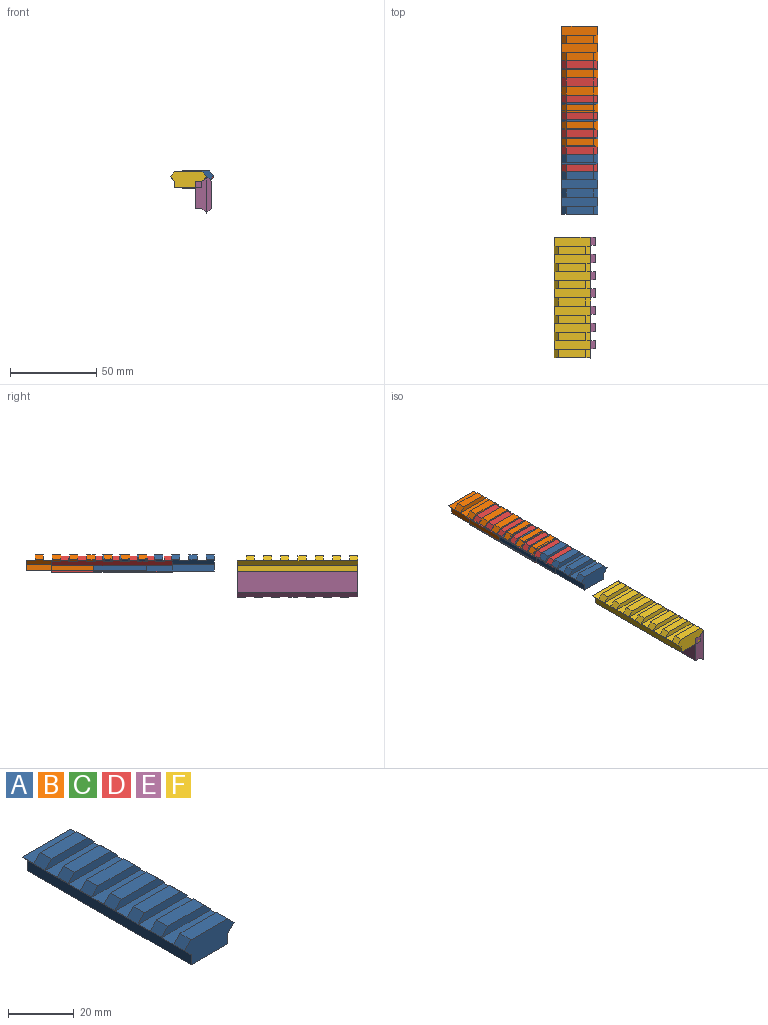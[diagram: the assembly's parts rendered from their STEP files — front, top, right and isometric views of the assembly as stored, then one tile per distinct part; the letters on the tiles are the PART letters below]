
ASSEMBLY  parts=6 mates=1
PART A: 48 faces, bbox 21.2x70x9.3 mm
  f0: plane 15.67x4.75mm, normal (0,0,1), area 74.4mm2, adj f8,f15,f42,f47
  f1: plane 15.67x4.75mm, normal (0,0,1), area 74.4mm2, adj f9,f16,f39,f44
  f2: plane 15.67x4.75mm, normal (0,0,1), area 74.4mm2, adj f10,f17,f36,f41
  f3: plane 15.67x4.75mm, normal (0,0,1), area 74.4mm2, adj f11,f18,f33,f38
  f4: plane 15.67x4.75mm, normal (0,0,1), area 74.4mm2, adj f13,f20,f28,f35
  f5: plane 15.67x4.75mm, normal (0,0,1), area 74.4mm2, adj f12,f19,f30,f32
  f6: plane 70x2.77mm, normal (0.71,0,-0.71), area 261.5mm2, adj f14,f15,f16,f17,f18,f19,f20,f22
  f7: plane 4.75x2.77mm, normal (-0.71,0,0.71), area 18.6mm2, adj f21,f22,f25,f45
  f8: plane 4.75x2.77mm, normal (-0.71,0,0.71), area 18.6mm2, adj f0,f21,f42,f47
  f9: plane 4.75x2.77mm, normal (-0.71,0,0.71), area 18.6mm2, adj f1,f21,f39,f44
  f10: plane 4.75x2.77mm, normal (-0.71,0,0.71), area 18.6mm2, adj f2,f21,f36,f41
  f11: plane 4.75x2.77mm, normal (-0.71,0,0.71), area 18.6mm2, adj f3,f21,f33,f38
  f12: plane 4.75x2.77mm, normal (-0.71,0,0.71), area 18.6mm2, adj f5,f21,f30,f32
  f13: plane 4.75x2.77mm, normal (-0.71,0,0.71), area 18.6mm2, adj f4,f21,f28,f35
  f14: plane 4.75x2.77mm, normal (0.71,0,0.71), area 18.6mm2, adj f6,f22,f25,f45
  f15: plane 4.75x2.77mm, normal (0.71,0,0.71), area 18.6mm2, adj f0,f6,f42,f47
  f16: plane 4.75x2.77mm, normal (0.71,0,0.71), area 18.6mm2, adj f1,f6,f39,f44
  f17: plane 4.75x2.77mm, normal (0.71,0,0.71), area 18.6mm2, adj f2,f6,f36,f41
  f18: plane 4.75x2.77mm, normal (0.71,0,0.71), area 18.6mm2, adj f3,f6,f33,f38
  f19: plane 4.75x2.77mm, normal (0.71,0,0.71), area 18.6mm2, adj f5,f6,f30,f32
  f20: plane 4.75x2.77mm, normal (0.71,0,0.71), area 18.6mm2, adj f4,f6,f28,f35
  f21: plane 70x2.77mm, normal (-0.71,0,-0.71), area 261.5mm2, adj f7,f8,f9,f10,f11,f12,f13,f22
  f22: plane 21.2x9.32mm, normal (0,-1,0), area 161.3mm2, adj f6,f7,f14,f21,f24,f25,f26,f27
  f23: plane 20.73x6.32mm, normal (0,1,0), area 105.4mm2, adj f6,f21,f24,f26,f27,f31
  f24: plane 70x15.67mm, normal (0,0,-1), area 1096.9mm2, adj f22,f23,f26,f27
  f25: plane 15.67x4.75mm, normal (0,0,1), area 74.4mm2, adj f7,f14,f22,f45
  f26: plane 70x3.79mm, normal (1,0,0), area 265.3mm2, adj f6,f22,f23,f24
  f27: plane 70x3.79mm, normal (-1,0,0), area 265.3mm2, adj f21,f22,f23,f24
  f28: plane 21.2x3mm, normal (0,1,0), area 55.9mm2, adj f4,f6,f13,f20,f21,f29
  f29: plane 20.73x5.25mm, normal (0,0,1), area 108.8mm2, adj f6,f21,f28,f30
  f30: plane 21.2x3mm, normal (0,-1,0), area 55.9mm2, adj f5,f6,f12,f19,f21,f29
  f31: plane 20.73x5.25mm, normal (0,0,1), area 108.8mm2, adj f6,f21,f23,f32
  f32: plane 21.2x3mm, normal (0,1,0), area 55.9mm2, adj f5,f6,f12,f19,f21,f31
  f33: plane 21.2x3mm, normal (0,1,0), area 55.9mm2, adj f3,f6,f11,f18,f21,f34
  f34: plane 20.73x5.25mm, normal (0,0,1), area 108.8mm2, adj f6,f21,f33,f35
  f35: plane 21.2x3mm, normal (0,-1,0), area 55.9mm2, adj f4,f6,f13,f20,f21,f34
  f36: plane 21.2x3mm, normal (0,1,0), area 55.9mm2, adj f2,f6,f10,f17,f21,f37
  f37: plane 20.73x5.25mm, normal (0,0,1), area 108.8mm2, adj f6,f21,f36,f38
  f38: plane 21.2x3mm, normal (0,-1,0), area 55.9mm2, adj f3,f6,f11,f18,f21,f37
  f39: plane 21.2x3mm, normal (0,1,0), area 55.9mm2, adj f1,f6,f9,f16,f21,f40
  f40: plane 20.73x5.25mm, normal (0,0,1), area 108.8mm2, adj f6,f21,f39,f41
  f41: plane 21.2x3mm, normal (0,-1,0), area 55.9mm2, adj f2,f6,f10,f17,f21,f40
  f42: plane 21.2x3mm, normal (0,1,0), area 55.9mm2, adj f0,f6,f8,f15,f21,f43
  f43: plane 20.73x5.25mm, normal (0,0,1), area 108.8mm2, adj f6,f21,f42,f44
  f44: plane 21.2x3mm, normal (0,-1,0), area 55.9mm2, adj f1,f6,f9,f16,f21,f43
  f45: plane 21.2x3mm, normal (0,1,0), area 55.9mm2, adj f6,f7,f14,f21,f25,f46
  f46: plane 20.73x5.25mm, normal (0,0,1), area 108.8mm2, adj f6,f21,f45,f47
  f47: plane 21.2x3mm, normal (0,-1,0), area 55.9mm2, adj f0,f6,f8,f15,f21,f46
PART B: same geometry as A
PART C: same geometry as A
PART D: same geometry as A
PART E: same geometry as A
PART F: same geometry as A
PLACE A t=(0,7.04,3.19)mm
PLACE B t=(0,46.16,3.25)mm
PLACE C t=(0,7.04,3.19)mm
PLACE D t=(0,31.32,2.54)mm
PLACE E rot(axis=(0.71,0,0.71),180deg) t=(-0.22,-146.12,-1.31)mm
PLACE F t=(-4.26,-76.12,2.73)mm
MATE fastened F.f6 <-> E.f6  axis (0.71,0,-0.71) through (3.57,-76.12,6.52)mm
